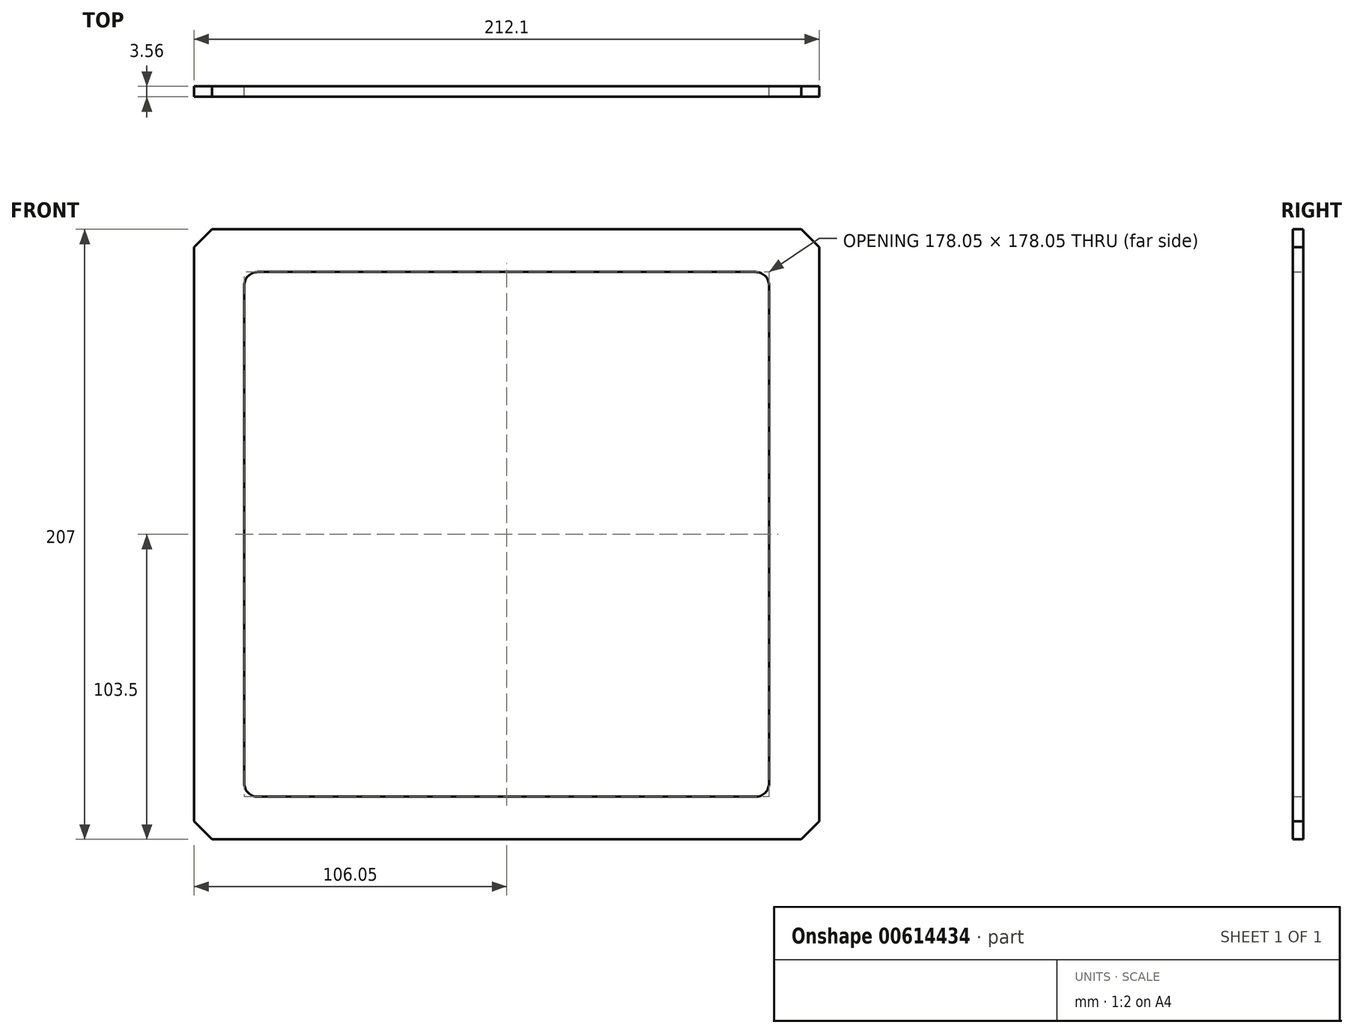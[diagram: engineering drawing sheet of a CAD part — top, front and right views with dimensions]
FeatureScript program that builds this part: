
annotation { "Feature Type Name" : "Feature", "Feature Type Description" : "" }
export const myFeature = defineFeature(function(context is Context, id is Id, definition is map)
    precondition{}
    {
        {
            var Q0;
            Q0=qCreatedBy(makeId("Front.planeOp"),FACE);
            var sketch = newSketch(context, id + "F0", { "sketchPlane" : qUnion([Q0])});
            skLineSegment(sketch, "E0.bottom", {"start": v(-106.05, -103.5) * mm, "end": v(106.05, -103.5) * mm});
            skLineSegment(sketch, "E0.top", {"start": v(-106.05, 103.5) * mm, "end": v(106.04, 103.5) * mm});
            skLineSegment(sketch, "E0.left", {"start": v(-106.05, -103.5) * mm, "end": v(-106.05, 103.5) * mm});
            skLineSegment(sketch, "E0.right", {"start": v(106.05, -103.5) * mm, "end": v(106.04, 103.5) * mm});
            skPoint(sketch, "E0.middle", {"position": v(0, 0) * mm});
            skLineSegment(sketch, "E1.bottom", {"start": v(-84.45, -89.03) * mm, "end": v(84.45, -89.03) * mm});
            skLineSegment(sketch, "E1.top", {"start": v(-84.45, 89.03) * mm, "end": v(84.45, 89.03) * mm});
            skLineSegment(sketch, "E1.left", {"start": v(-89.03, -84.46) * mm, "end": v(-89.03, 84.46) * mm});
            skLineSegment(sketch, "E1.right", {"start": v(89.03, -84.46) * mm, "end": v(89.03, 84.46) * mm});
            skPoint(sketch, "E2.visualSharp", {"position": v(-89.03, 89.03) * mm});
            skArc(sketch, "E2.filletArc", {"start": v(-84.45, 89.03) * mm, "mid": v(-87.69, 87.69) * mm, "end": v(-89.03, 84.46) * mm});
            skPoint(sketch, "E3.visualSharp", {"position": v(89.03, 89.03) * mm});
            skArc(sketch, "E3.filletArc", {"start": v(89.03, 84.46) * mm, "mid": v(87.69, 87.69) * mm, "end": v(84.45, 89.03) * mm});
            skPoint(sketch, "E4.visualSharp", {"position": v(89.03, -89.03) * mm});
            skArc(sketch, "E4.filletArc", {"start": v(84.45, -89.03) * mm, "mid": v(87.69, -87.69) * mm, "end": v(89.03, -84.46) * mm});
            skPoint(sketch, "E5.visualSharp", {"position": v(-89.03, -89.03) * mm});
            skArc(sketch, "E5.filletArc", {"start": v(-89.03, -84.46) * mm, "mid": v(-87.69, -87.69) * mm, "end": v(-84.45, -89.03) * mm});
            skSolve(sketch);
        }
        {
            var Q0;
            Q0=makeQuery(id+"F0.imprint","IMPRINT",FACE,{"disambiguationData":[TD([[makeQuery(id+"F0.imprint","IMPRINT",EDGE,{"derivedFrom":sQuery(id+"F0.wireOp",EDGE,"E0.bottom")}),1.0]])]});
            extrude(context, id + "F1", {"entities" : qUnion([Q0]), "depth" : 3.56 * mm});
        }
        {
            var Q0;
            Q0=makeQuery(id+"F1.opExtrude","SWEPT_EDGE",EDGE,{"disambiguationData":[OSD([sQuery(id+"F0.wireOp",EDGE,"E0.top"),sQuery(id+"F0.wireOp",EDGE,"E0.left")])]});
            var Q1;
            Q1=makeQuery(id+"F1.opExtrude","SWEPT_EDGE",EDGE,{"disambiguationData":[OSD([sQuery(id+"F0.wireOp",EDGE,"E0.top"),sQuery(id+"F0.wireOp",EDGE,"E0.right")])]});
            var Q2;
            Q2=makeQuery(id+"F1.opExtrude","SWEPT_EDGE",EDGE,{"disambiguationData":[OSD([sQuery(id+"F0.wireOp",EDGE,"E0.bottom"),sQuery(id+"F0.wireOp",EDGE,"E0.right")])]});
            var Q3;
            Q3=makeQuery(id+"F1.opExtrude","SWEPT_EDGE",EDGE,{"disambiguationData":[OSD([sQuery(id+"F0.wireOp",EDGE,"E0.bottom"),sQuery(id+"F0.wireOp",EDGE,"E0.left")])]});
            chamfer(context, id + "F2", {"entities" : qUnion([Q0, Q1, Q2, Q3]), "width" : 6.1 * mm, "tangentPropagation" : true});
        }
    });
